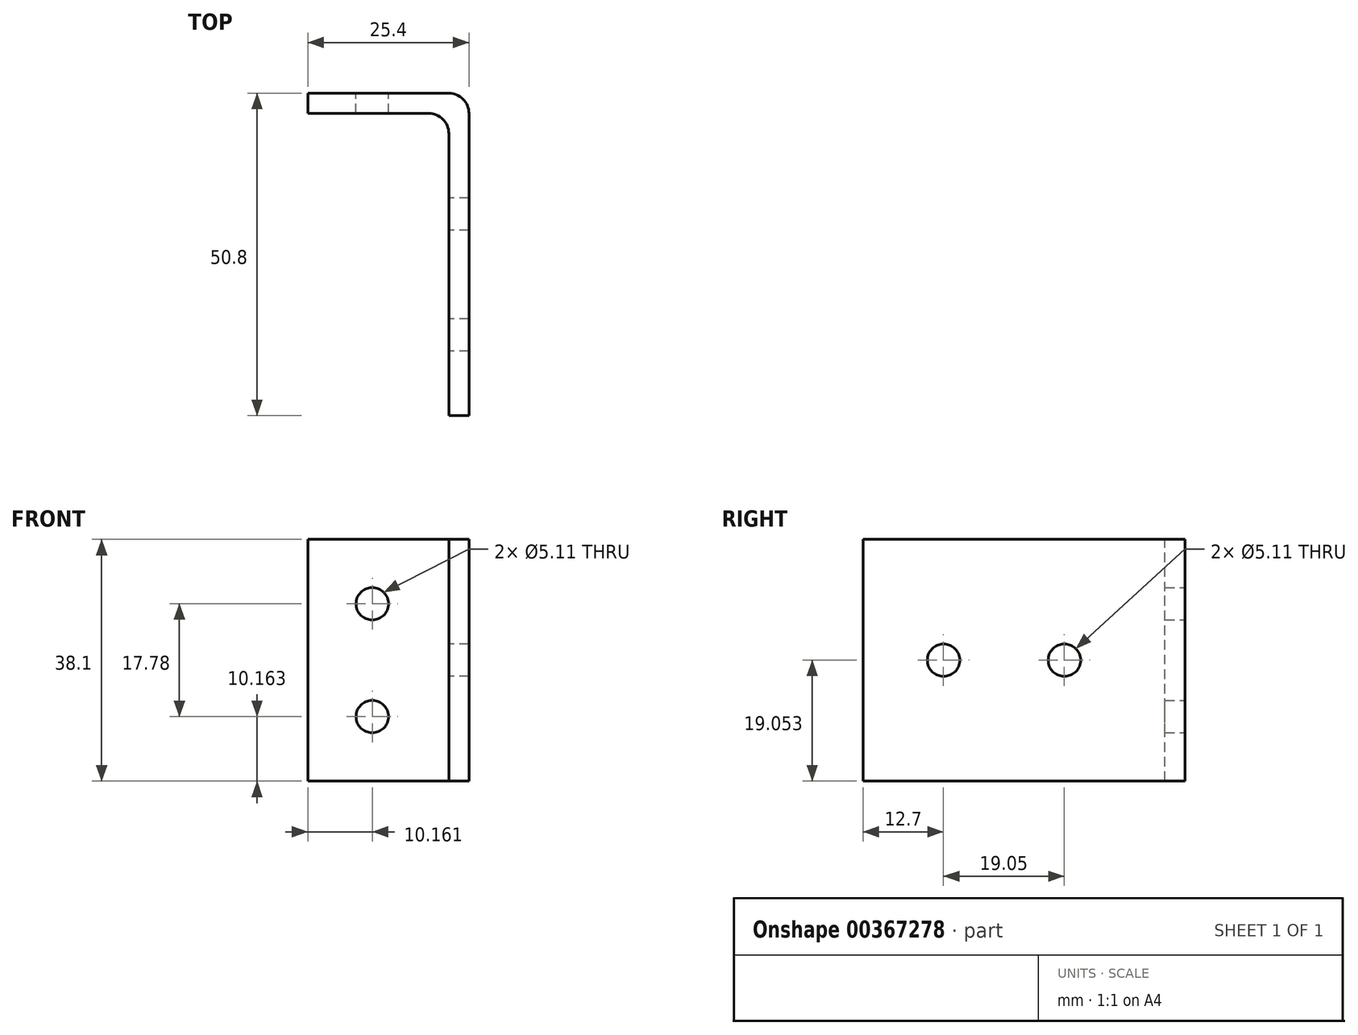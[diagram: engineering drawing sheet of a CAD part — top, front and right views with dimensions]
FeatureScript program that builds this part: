
annotation { "Feature Type Name" : "Feature", "Feature Type Description" : "" }
export const myFeature = defineFeature(function(context is Context, id is Id, definition is map)
    precondition{}
    {
        {
            var Q0;
            Q0=qCreatedBy(makeId("Front.planeOp"),FACE);
            var sketch = newSketch(context, id + "F0", { "sketchPlane" : qUnion([Q0])});
            skLineSegment(sketch, "E0.bottom", {"start": v(-11.9, 35) * mm, "end": v(13.5, 35) * mm});
            skLineSegment(sketch, "E0.top", {"start": v(-11.9, -3.1) * mm, "end": v(13.5, -3.1) * mm});
            skLineSegment(sketch, "E0.left", {"start": v(-11.9, 35) * mm, "end": v(-11.9, -3.1) * mm});
            skLineSegment(sketch, "E0.right", {"start": v(13.5, 35) * mm, "end": v(13.5, -3.1) * mm});
            skPoint(sketch, "E1", {"position": v(-1.75, 24.84) * mm});
            skPoint(sketch, "E2", {"position": v(-1.75, 7.06) * mm});
            skLineSegment(sketch, "E3", {"start": v(10.32, 35) * mm, "end": v(10.32, -3.1) * mm});
            skSolve(sketch);
        }
        {
            var Q0;
            Q0=makeQuery(id+"F0.imprint","IMPRINT",FACE,{"disambiguationData":[TD([[makeQuery(id+"F0.imprint","IMPRINT",EDGE,{"derivedFrom":sQuery(id+"F0.wireOp",EDGE,"E0.bottom")}),-1.0]])]});
            extrude(context, id + "F1", {"entities" : qUnion([Q0]), "depth" : 3.17 * mm});
        }
        {
            var Q0;
            Q0=sQuery(id+"F0.wireOp",VERTEX,"E1");
            var Q1;
            Q1=sQuery(id+"F0.wireOp",VERTEX,"E2");
            var Q2;
            Q2=makeQuery(id+"F1.opExtrude","SWEPT_BODY",BODY,{"disambiguationData":[OSD([sQuery(id+"F0.wireOp",EDGE,"E0.bottom"),sQuery(id+"F0.wireOp",EDGE,"E0.top"),sQuery(id+"F0.wireOp",EDGE,"E0.left"),sQuery(id+"F0.wireOp",EDGE,"E0.right")])]});
            hole(context, id + "F2", {"style" : HoleStyle.SIMPLE, "endStyle" : HoleEndStyle.THROUGH, "oppositeDirection" : true, "holeDiameter" : 5.1 * mm, "isTappedThrough" : true, "tappedDepth" : 12.7 * mm, "tapClearance" : 3, "locations" : qUnion([Q0, Q1]), "scope" : qUnion([Q2])});
        }
        {
            var Q0;
            {var subQ0=sQuery(id+"F0.wireOp",EDGE,"E0.right");Q0=makeQuery(id+"F0.imprint","IMPRINT",FACE,{"disambiguationData":[TD([[makeQuery(id+"F0.imprint","IMPRINT",EDGE,{"derivedFrom":subQ0}),-1.0]])]});}
            extrude(context, id + "F3", {"entities" : qUnion([Q0]), "operationType" : NewBodyOperationType.ADD, "depth" : 50.8 * mm});
        }
        {
            var Q0;
            Q0=makeQuery(id+"F3.boolean.opBoolean","INTERSECT",EDGE,{"derivedFrom":[makeQuery(id+"F1.opExtrude","CAP_FACE",FACE,{"disambiguationData":[OSD([sQuery(id+"F0.wireOp",EDGE,"E0.bottom"),sQuery(id+"F0.wireOp",EDGE,"E0.top"),sQuery(id+"F0.wireOp",EDGE,"E0.left"),sQuery(id+"F0.wireOp",EDGE,"E0.right")])],"isStart":false}),makeQuery(id+"F3.opExtrude","SWEPT_FACE",FACE,{"disambiguationData":[OSD([sQuery(id+"F0.wireOp",EDGE,"E3")])]})]});
            var Q1;
            Q1=makeQuery(id+"F1.opExtrude","CAP_EDGE",EDGE,{"disambiguationData":[OSD([sQuery(id+"F0.wireOp",EDGE,"E0.right")])],"isStart":true});
            fillet(context, id + "F4", {"entities" : qUnion([Q0, Q1]), "radius" : 3.17 * mm, "tangentPropagation" : true, "allowEdgeOverflow" : false});
        }
        {
            var Q0;
            Q0=makeQuery(id+"F3.opExtrude","SWEPT_FACE",FACE,{"disambiguationData":[OSD([sQuery(id+"F0.wireOp",EDGE,"E3")])]});
            var sketch = newSketch(context, id + "F5", { "sketchPlane" : qUnion([Q0])});
            skPoint(sketch, "E4", {"position": v(38.1, 15.95) * mm});
            skPoint(sketch, "E5", {"position": v(19.05, 15.95) * mm});
            skSolve(sketch);
        }
        {
            var Q0;
            Q0=sQuery(id+"F5.wireOp",VERTEX,"E5");
            var Q1;
            Q1=sQuery(id+"F5.wireOp",VERTEX,"E4");
            var Q2;
            Q2=makeQuery(id+"F1.opExtrude","SWEPT_BODY",BODY,{"disambiguationData":[OSD([sQuery(id+"F0.wireOp",EDGE,"E0.bottom"),sQuery(id+"F0.wireOp",EDGE,"E0.top"),sQuery(id+"F0.wireOp",EDGE,"E0.left"),sQuery(id+"F0.wireOp",EDGE,"E0.right")])]});
            hole(context, id + "F6", {"style" : HoleStyle.SIMPLE, "endStyle" : HoleEndStyle.THROUGH, "holeDiameter" : 5.1 * mm, "isTappedThrough" : true, "tappedDepth" : 12.7 * mm, "tapClearance" : 3, "locations" : qUnion([Q0, Q1]), "scope" : qUnion([Q2])});
        }
    });
